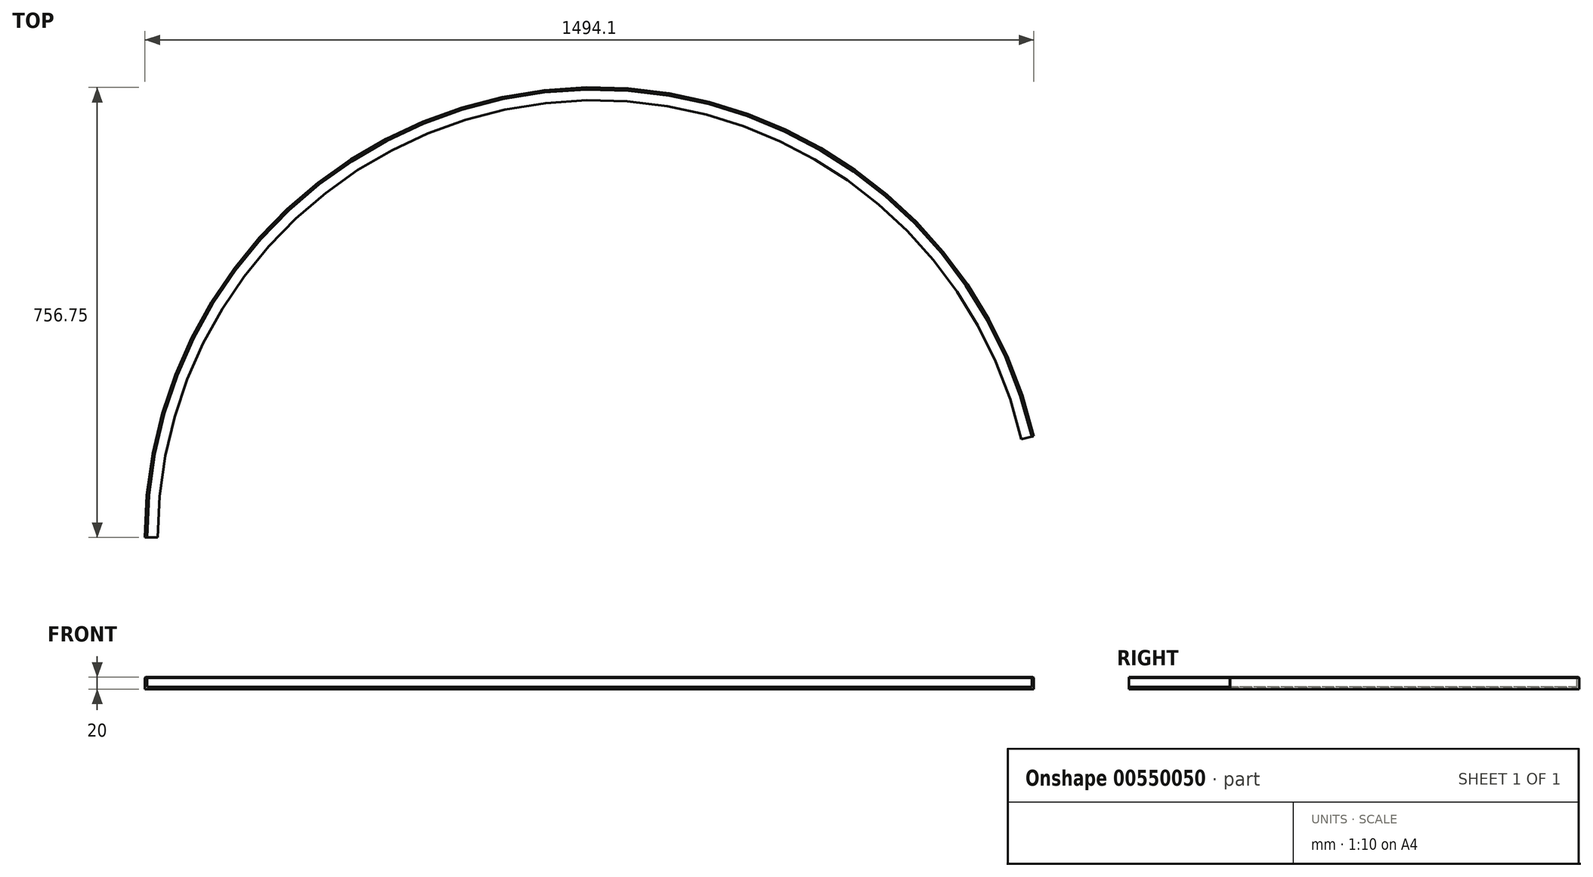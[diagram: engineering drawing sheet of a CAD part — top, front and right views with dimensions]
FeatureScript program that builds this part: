
annotation { "Feature Type Name" : "Feature", "Feature Type Description" : "" }
export const myFeature = defineFeature(function(context is Context, id is Id, definition is map)
    precondition{}
    {
        {
            var Q0;
            Q0=qCreatedBy(makeId("Top.planeOp"),FACE);
            var sketch = newSketch(context, id + "F0", { "sketchPlane" : qUnion([Q0])});
            skArc(sketch, "E0", {"start": v(-755, 0) * mm, "mid": v(-360.43, 663.41) * mm, "end": v(410.88, 633.4) * mm, "construction": true});
            skSolve(sketch);
        }
        {
            var Q0;
            Q0=qCreatedBy(makeId("Front.planeOp"),FACE);
            var sketch = newSketch(context, id + "F1", { "sketchPlane" : qUnion([Q0])});
            skLineSegment(sketch, "E1", {"start": v(0, -8.67) * mm, "end": v(0, 24.04) * mm});
            skSolve(sketch);
        }
        {
            var Q0;
            Q0=qCreatedBy(makeId("Front.planeOp"),FACE);
            var sketch = newSketch(context, id + "F2", { "sketchPlane" : qUnion([Q0])});
            skLineSegment(sketch, "E2", {"start": v(-756.75, 20) * mm, "end": v(-753.25, 20) * mm});
            skLineSegment(sketch, "E3", {"start": v(-753.25, 20) * mm, "end": v(-753.25, 3.5) * mm});
            skLineSegment(sketch, "E4", {"start": v(-753.25, 3.5) * mm, "end": v(-735.25, 3.5) * mm});
            skLineSegment(sketch, "E5", {"start": v(-735.25, 3.5) * mm, "end": v(-735.25, 0) * mm});
            skLineSegment(sketch, "E6", {"start": v(-755, 20) * mm, "end": v(-755, 0) * mm, "construction": true});
            skLineSegment(sketch, "E7", {"start": v(-735.25, 0) * mm, "end": v(-756.75, 0) * mm});
            skLineSegment(sketch, "E8", {"start": v(-756.75, 0) * mm, "end": v(-756.75, 20) * mm});
            skSolve(sketch);
        }
        {
            var Q0;
            Q0=makeQuery(id+"F2.imprint","IMPRINT",FACE,{"disambiguationData":[TD([[makeQuery(id+"F2.imprint","IMPRINT",EDGE,{"derivedFrom":sQuery(id+"F2.wireOp",EDGE,"gnxbdt0V-2acl-EAl1-C6b3-It5QXxdKtF35")}),-1.0]])]});
            var Q1;
            Q1=makeQuery(id+"F2.imprint","IMPRINT",FACE,{"disambiguationData":[TD([[makeQuery(id+"F2.imprint","IMPRINT",EDGE,{"derivedFrom":sQuery(id+"F2.wireOp",EDGE,"E2")}),-1.0]])]});
            var Q2;
            Q2=sQuery(id+"F1.wireOp",EDGE,"E1");
            revolve(context, id + "F3", {"entities" : qUnion([Q0, Q1]), "axis" : qUnion([Q2]), "revolveType" : RevolveType.ONE_DIRECTION, "oppositeDirection" : true, "angle" : 167 * degree, "surfaceOperationType" : NewSurfaceOperationType.NEW});
        }
        {
            var Q0;
            Q0=makeQuery(id+"F3.opRevolve","SWEPT_EDGE",EDGE,{"disambiguationData":[OSD([sQuery(id+"F2.wireOp",EDGE,"E2"),sQuery(id+"F2.wireOp",EDGE,"E8")])]});
            var Q1;
            Q1=makeQuery(id+"F3.opRevolve","SWEPT_EDGE",EDGE,{"disambiguationData":[OSD([sQuery(id+"F2.wireOp",EDGE,"E2"),sQuery(id+"F2.wireOp",EDGE,"E3")])]});
            chamfer(context, id + "F4", {"entities" : qUnion([Q0, Q1]), "width" : 1 * mm, "tangentPropagation" : true});
        }
    });
